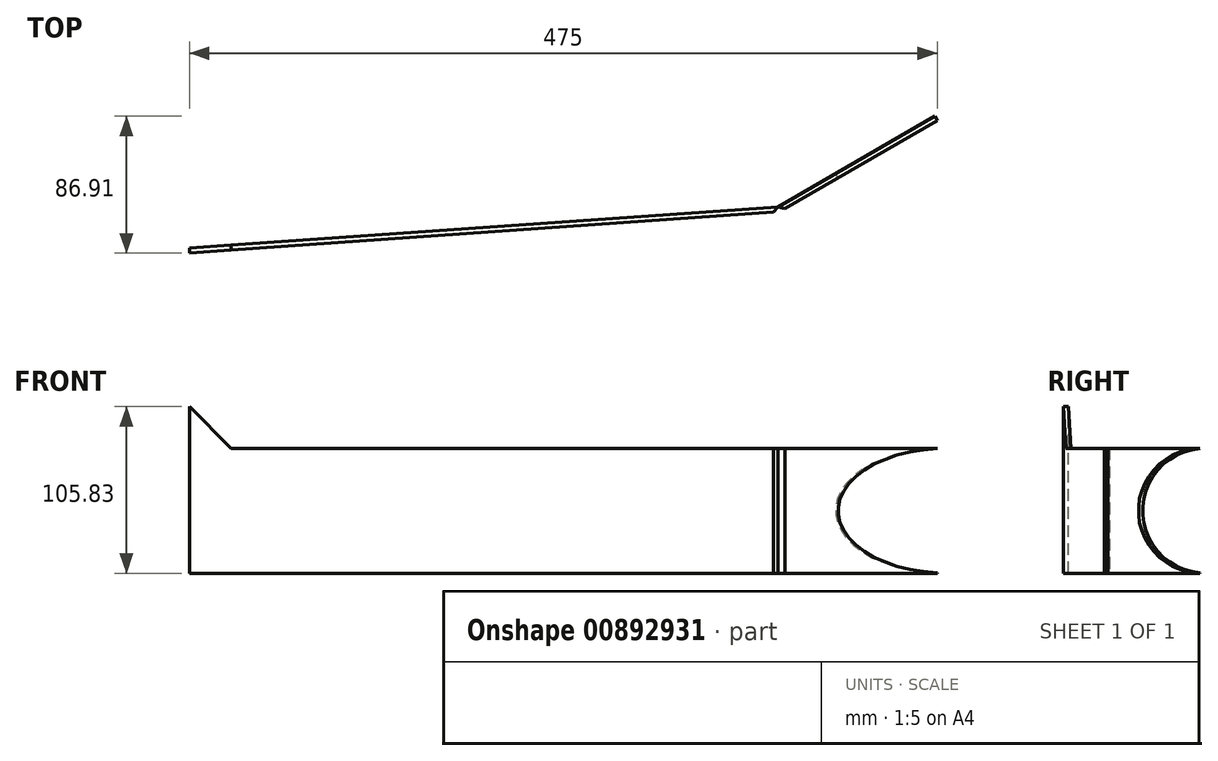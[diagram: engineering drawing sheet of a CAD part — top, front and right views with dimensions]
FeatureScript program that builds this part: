
annotation { "Feature Type Name" : "Feature", "Feature Type Description" : "" }
export const myFeature = defineFeature(function(context is Context, id is Id, definition is map)
    precondition{}
    {
        {
            var Q0;
            Q0=qCreatedBy(makeId("Top.planeOp"),FACE);
            var sketch = newSketch(context, id + "F0", { "sketchPlane" : qUnion([Q0])});
            skLineSegment(sketch, "E0", {"start": v(478.92, 47.23) * mm, "end": v(478.92, -917.97) * mm, "construction": true});
            skLineSegment(sketch, "E1", {"start": v(478.92, -917.97) * mm, "end": v(390.02, -917.97) * mm, "construction": true});
            skLineSegment(sketch, "E2", {"start": v(-54.63, -3.84) * mm, "end": v(390.02, -917.97) * mm, "construction": true});
            skLineSegment(sketch, "E3", {"start": v(-79.5, 47.23) * mm, "end": v(-79.5, 86.91) * mm});
            skCircle(sketch, "E4", {"center": v(-38.37, 20.63) * mm, "radius": 22.23 * mm});
            skLineSegment(sketch, "E5.0", {"start": v(478.92, 86.91) * mm, "end": v(-79.5, 86.91) * mm});
            skLineSegment(sketch, "E6", {"start": v(-79.5, 47.23) * mm, "end": v(-54.63, -3.84) * mm});
            skLineSegment(sketch, "E7", {"start": v(-79.5, 47.23) * mm, "end": v(410.18, 47.23) * mm});
            skLineSegment(sketch, "E8", {"start": v(478.92, 86.91) * mm, "end": v(478.92, 47.23) * mm});
            skLineSegment(sketch, "E9", {"start": v(-54.63, -3.84) * mm, "end": v(373.86, 26.26) * mm});
            skCircle(sketch, "E10", {"center": v(-38.37, 20.63) * mm, "radius": 6.35 * mm});
            skLineSegment(sketch, "E11", {"start": v(478.92, 86.91) * mm, "end": v(373.86, 26.26) * mm});
            skLineSegment(sketch, "E12", {"start": v(-38.22, 78.5) * mm, "end": v(0, 0) * mm});
            skLineSegment(sketch, "E13", {"start": v(-38.22, 78.5) * mm, "end": v(-38.22, 86.91) * mm});
            skSolve(sketch);
        }
        {
            var Q0;
            Q0=sQuery(id+"F0.wireOp",EDGE,"E9");
            cPlane(context, id + "F1", {"entities" : qUnion([Q0]), "cplaneType" : CPlaneType.LINE_ANGLE, "offset" : 25.4 * mm, "angle" : 0 * degree, "oppositeDirection" : true, "width" : 152.4 * mm, "height" : 152.4 * mm});
        }
        {
            var Q0;
            Q0=qCreatedBy(id+"F1.planeOp",FACE);
            var sketch = newSketch(context, id + "F2", { "sketchPlane" : qUnion([Q0])});
            skLineSegment(sketch, "E14", {"start": v(-374.78, 0) * mm, "end": v(0, 0) * mm});
            skLineSegment(sketch, "E15.MirrorCS", {"start": v(-374.78, 79.38) * mm, "end": v(-374.78, 0) * mm});
            skLineSegment(sketch, "E16.MirrorCS", {"start": v(-26.46, 79.37) * mm, "end": v(-374.78, 79.37) * mm});
            skLineSegment(sketch, "E17.MirrorCS", {"start": v(0, 105.83) * mm, "end": v(-26.46, 79.37) * mm});
            skLineSegment(sketch, "E18.MirrorCS", {"start": v(0, 0) * mm, "end": v(0, 105.83) * mm});
            skPoint(sketch, "E19.0", {"position": v(-374.78, 0) * mm});
            skSolve(sketch);
        }
        {
            var Q0;
            Q0=makeQuery(id+"F2.imprint","IMPRINT",FACE,{"disambiguationData":[TD([[makeQuery(id+"F2.imprint","IMPRINT",EDGE,{"derivedFrom":sQuery(id+"F2.wireOp",EDGE,"E14")}),1.0]])]});
            extrude(context, id + "F3", {"entities" : qUnion([Q0]), "oppositeDirection" : true, "depth" : 3.17 * mm, "offsetDistance" : 25.4 * mm});
        }
        {
            var Q0;
            Q0=sQuery(id+"F0.wireOp",EDGE,"E11");
            cPlane(context, id + "F4", {"entities" : qUnion([Q0]), "cplaneType" : CPlaneType.LINE_ANGLE, "offset" : 25.4 * mm, "angle" : 0 * degree, "width" : 152.4 * mm, "height" : 152.4 * mm});
        }
        {
            var Q0;
            Q0=qCreatedBy(id+"F4.planeOp",FACE);
            var sketch = newSketch(context, id + "F5", { "sketchPlane" : qUnion([Q0])});
            skPoint(sketch, "E20.0", {"position": v(336.9, 0) * mm});
            skPoint(sketch, "E21.0", {"position": v(336.9, 79.38) * mm});
            skPoint(sketch, "E22.0", {"position": v(458.21, 0) * mm});
            skLineSegment(sketch, "E23", {"start": v(458.21, 0) * mm, "end": v(336.9, 0) * mm});
            skLineSegment(sketch, "E24", {"start": v(336.9, 79.38) * mm, "end": v(458.21, 79.38) * mm});
            skLineSegment(sketch, "E25", {"start": v(458.21, 79.38) * mm, "end": v(458.21, 0) * mm});
            skLineSegment(sketch, "E26", {"start": v(336.9, 79.38) * mm, "end": v(336.9, 0) * mm});
            skSolve(sketch);
        }
        {
            var Q0;
            Q0=makeQuery(id+"F5.imprint","IMPRINT",FACE,{"disambiguationData":[TD([[makeQuery(id+"F5.imprint","IMPRINT",EDGE,{"derivedFrom":sQuery(id+"F5.wireOp",EDGE,"E23")}),-1.0]])]});
            extrude(context, id + "F6", {"entities" : qUnion([Q0]), "depth" : 3.17 * mm, "offsetDistance" : 25.4 * mm});
        }
        {
            var Q0;
            Q0=makeQuery(id+"F6.opExtrude","SWEPT_FACE",FACE,{"disambiguationData":[OSD([sQuery(id+"F5.wireOp",EDGE,"E24")])]});
            cPlane(context, id + "F7", {"entities" : qUnion([Q0]), "cplaneType" : CPlaneType.OFFSET, "offset" : 25.4 * mm, "width" : 152.4 * mm, "height" : 152.4 * mm});
        }
        {
            var Q0;
            Q0=qCreatedBy(id+"F7.planeOp",FACE);
            var sketch = newSketch(context, id + "F8", { "sketchPlane" : qUnion([Q0])});
            skPoint(sketch, "E27.0", {"position": v(373.86, 26.26) * mm});
            skLineSegment(sketch, "E28.0", {"start": v(375.45, 23.5) * mm, "end": v(480.5, 84.16) * mm});
            skLineSegment(sketch, "E29.0", {"start": v(26.62, -1.31) * mm, "end": v(374.08, 23.1) * mm});
            skLineSegment(sketch, "E30", {"start": v(373.86, 26.26) * mm, "end": v(370.81, 22.86) * mm});
            skLineSegment(sketch, "E31", {"start": v(373.13, 23.02) * mm, "end": v(374.08, 23.1) * mm});
            skLineSegment(sketch, "E32", {"start": v(378.3, 25.16) * mm, "end": v(373.86, 26.26) * mm});
            skLineSegment(sketch, "E33", {"start": v(375.45, 23.5) * mm, "end": v(374.08, 23.1) * mm});
            skLineSegment(sketch, "E34", {"start": v(370.81, 22.86) * mm, "end": v(373.13, 23.02) * mm});
            skLineSegment(sketch, "E35", {"start": v(374.08, 23.1) * mm, "end": v(375.45, 23.5) * mm});
            skSolve(sketch);
        }
        {
            var Q0;
            Q0=makeQuery(id+"F8.imprint","IMPRINT",FACE,{"disambiguationData":[TD([[makeQuery(id+"F8.imprint","IMPRINT",EDGE,{"derivedFrom":sQuery(id+"F8.wireOp",EDGE,"E30")}),1.0]])]});
            extrude(context, id + "F9", {"entities" : qUnion([Q0]), "operationType" : NewBodyOperationType.REMOVE, "oppositeDirection" : true, "depth" : 508 * mm, "offsetDistance" : 25.4 * mm});
        }
        {
            var Q0;
            Q0=makeQuery(id+"F6.opExtrude","CAP_EDGE",EDGE,{"disambiguationData":[OSD([sQuery(id+"F5.wireOp",EDGE,"E25")])],"isStart":true});
            cPlane(context, id + "F10", {"entities" : qUnion([Q0]), "cplaneType" : CPlaneType.LINE_ANGLE, "offset" : 25.4 * mm, "angle" : 0 * degree, "width" : 152.4 * mm, "height" : 152.4 * mm});
        }
        {
            var Q0;
            Q0=qCreatedBy(id+"F10.planeOp",FACE);
            var sketch = newSketch(context, id + "F11", { "sketchPlane" : qUnion([Q0])});
            skLineSegment(sketch, "E36.0", {"start": v(-86.91, 79.38) * mm, "end": v(-86.91, 0) * mm});
            skCircle(sketch, "E37", {"center": v(-86.91, 39.69) * mm, "radius": 39.69 * mm});
            skSolve(sketch);
        }
        {
            var Q0;
            {var subQ0=sQuery(id+"F11.wireOp",EDGE,"E36.0");Q0=makeQuery(id+"F11.imprint","IMPRINT",FACE,{"disambiguationData":[TD([[makeQuery(id+"F11.imprint","IMPRINT",EDGE,{"derivedFrom":subQ0}),1.0]])]});}
            var Q1;
            {var subQ0=sQuery(id+"F11.wireOp",EDGE,"E36.0");Q1=makeQuery(id+"F11.imprint","IMPRINT",FACE,{"disambiguationData":[TD([[makeQuery(id+"F11.imprint","IMPRINT",EDGE,{"derivedFrom":subQ0}),-1.0]])]});}
            extrude(context, id + "F12", {"entities" : qUnion([Q0, Q1]), "operationType" : NewBodyOperationType.REMOVE, "endBound" : BoundingType.SYMMETRIC, "depth" : 254 * mm, "offsetDistance" : 25.4 * mm});
        }
        {
            var Q0;
            Q0=makeQuery(id+"F6.opExtrude","CAP_FACE",FACE,{"disambiguationData":[OSD([sQuery(id+"F5.wireOp",EDGE,"E23"),sQuery(id+"F5.wireOp",EDGE,"E24"),sQuery(id+"F5.wireOp",EDGE,"E25"),sQuery(id+"F5.wireOp",EDGE,"E26")])],"isStart":true});
            cPlane(context, id + "F13", {"entities" : qUnion([Q0]), "cplaneType" : CPlaneType.OFFSET, "offset" : 0 * mm, "width" : 152.4 * mm, "height" : 152.4 * mm});
        }
        {
            var Q0;
            Q0=qCreatedBy(id+"F13.planeOp",FACE);
            var sketch = newSketch(context, id + "F14", { "sketchPlane" : qUnion([Q0])});
            skPoint(sketch, "E38.0", {"position": v(-458.21, 79.38) * mm});
            skLineSegment(sketch, "E39", {"start": v(-458.21, 79.38) * mm, "end": v(-458.21, 85.72) * mm, "construction": true});
            skLineSegment(sketch, "E40", {"start": v(-458.21, 85.72) * mm, "end": v(-451.86, 85.72) * mm, "construction": true});
            skLineSegment(sketch, "E41", {"start": v(-451.86, 85.72) * mm, "end": v(-451.86, -16.69) * mm});
            skLineSegment(sketch, "E42", {"start": v(-451.86, -16.69) * mm, "end": v(-474.48, -16.69) * mm});
            skLineSegment(sketch, "E43", {"start": v(-474.48, -16.69) * mm, "end": v(-474.48, 85.72) * mm});
            skLineSegment(sketch, "E44", {"start": v(-474.48, 85.72) * mm, "end": v(-451.86, 85.72) * mm});
            skSolve(sketch);
        }
        {
            var Q0;
            Q0=makeQuery(id+"F14.imprint","IMPRINT",FACE,{"disambiguationData":[TD([[makeQuery(id+"F14.imprint","IMPRINT",EDGE,{"derivedFrom":sQuery(id+"F14.wireOp",EDGE,"E41")}),-1.0]])]});
            extrude(context, id + "F15", {"entities" : qUnion([Q0]), "operationType" : NewBodyOperationType.REMOVE, "endBound" : BoundingType.THROUGH_ALL, "oppositeDirection" : true, "depth" : 25.4 * mm, "offsetDistance" : 25.4 * mm});
        }
        {
            var Q0;
            Q0=qCreatedBy(id+"F13.planeOp",FACE);
            var sketch = newSketch(context, id + "F16", { "sketchPlane" : qUnion([Q0])});
            skPoint(sketch, "E45.0", {"position": v(-451.86, 0.13) * mm});
            skEllipticalArc(sketch, "E46.0", {});
            skPoint(sketch, "E47.0", {"position": v(-451.86, 79.25) * mm});
            skLineSegment(sketch, "E48", {"start": v(-451.86, 0.13) * mm, "end": v(-465.68, 0.13) * mm});
            skLineSegment(sketch, "E49", {"start": v(-465.68, 0.13) * mm, "end": v(-465.68, 79.25) * mm});
            skLineSegment(sketch, "E50", {"start": v(-465.68, 79.25) * mm, "end": v(-451.86, 79.25) * mm});
            const initialGuessF16  = {"E46.0": [-0.4582111025642435, 0.0396875, -1, 0, 0.079375, 0.0396875, 1.6508819068285554, 4.632303400351032]};
            skSetInitialGuess(sketch, initialGuessF16);
            skSolve(sketch);
        }
        {
            var Q0;
            Q0=makeQuery(id+"F16.imprint","IMPRINT",FACE,{"disambiguationData":[TD([[makeQuery(id+"F16.imprint","IMPRINT",EDGE,{"derivedFrom":sQuery(id+"F16.wireOp",EDGE,"E46.0")}),1.0]])]});
            extrude(context, id + "F17", {"entities" : qUnion([Q0]), "operationType" : NewBodyOperationType.REMOVE, "endBound" : BoundingType.THROUGH_ALL, "oppositeDirection" : true, "depth" : 25.4 * mm, "offsetDistance" : 25.4 * mm});
        }
    });
